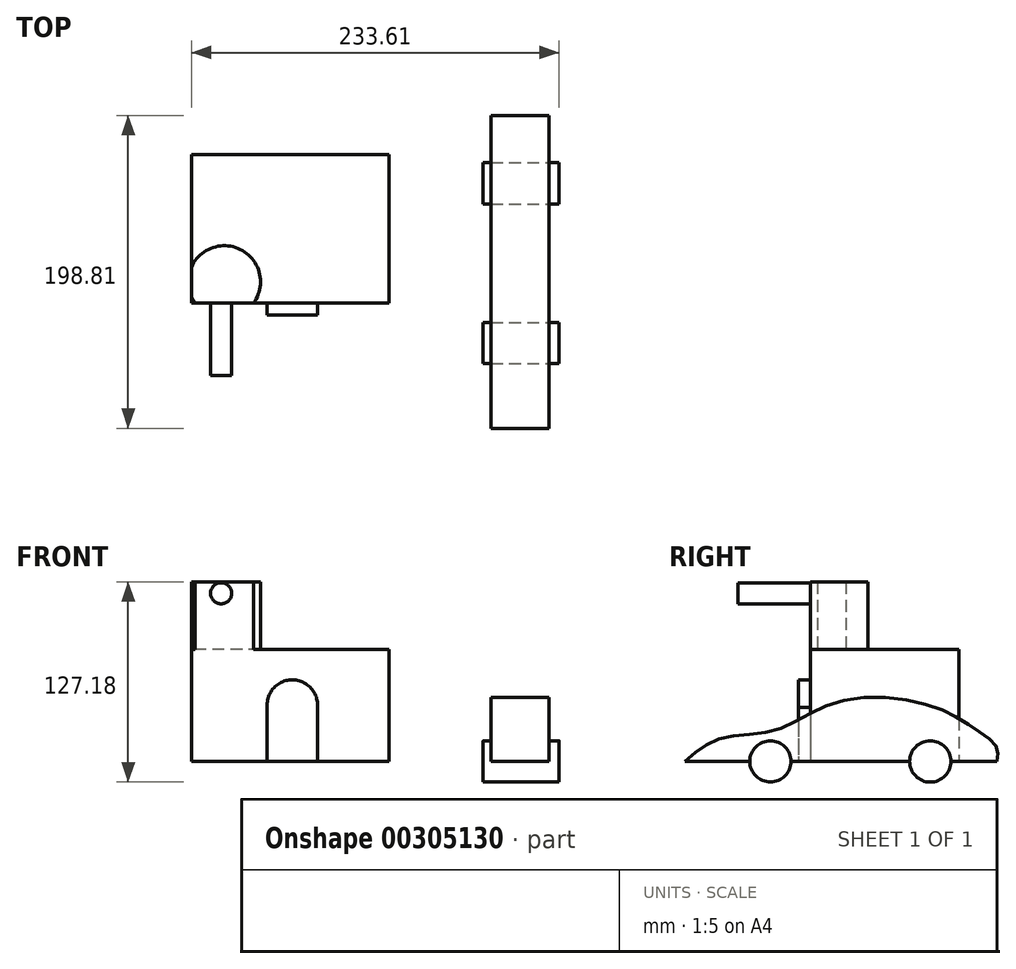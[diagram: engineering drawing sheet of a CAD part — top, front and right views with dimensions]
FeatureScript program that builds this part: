
annotation { "Feature Type Name" : "Feature", "Feature Type Description" : "" }
export const myFeature = defineFeature(function(context is Context, id is Id, definition is map)
    precondition{}
    {
        {
            var Q0;
            Q0=qCreatedBy(makeId("Top.planeOp"),FACE);
            var sketch = newSketch(context, id + "F0", { "sketchPlane" : qUnion([Q0])});
            skLineSegment(sketch, "E0.bottom", {"start": v(-64.2, 55.75) * mm, "end": v(61.5, 55.75) * mm});
            skLineSegment(sketch, "E0.top", {"start": v(-64.2, -38.63) * mm, "end": v(61.5, -38.63) * mm});
            skLineSegment(sketch, "E0.left", {"start": v(-64.2, 55.75) * mm, "end": v(-64.2, -38.63) * mm});
            skLineSegment(sketch, "E0.right", {"start": v(61.5, 55.75) * mm, "end": v(61.5, -38.63) * mm});
            skSolve(sketch);
        }
        {
            var Q0;
            Q0=makeQuery(id+"F0.imprint","IMPRINT",FACE,{"disambiguationData":[TD([[makeQuery(id+"F0.imprint","IMPRINT",EDGE,{"derivedFrom":sQuery(id+"F0.wireOp",EDGE,"E0.bottom")}),-1.0]])]});
            extrude(context, id + "F1", {"entities" : qUnion([Q0]), "depth" : 71.12 * mm});
        }
        {
            var Q0;
            Q0=makeQuery(id+"F1.opExtrude","SWEPT_FACE",FACE,{"disambiguationData":[OSD([sQuery(id+"F0.wireOp",EDGE,"E0.top")])]});
            var sketch = newSketch(context, id + "F2", { "sketchPlane" : qUnion([Q0])});
            skArc(sketch, "E1", {"start": v(15.92, 34.3) * mm, "mid": v(0.16, 51.86) * mm, "end": v(-15.95, 34.61) * mm});
            skLineSegment(sketch, "E2", {"start": v(-15.95, 37.12) * mm, "end": v(-15.95, 0) * mm});
            skLineSegment(sketch, "E3", {"start": v(15.92, 37.44) * mm, "end": v(15.92, 0) * mm});
            skLineSegment(sketch, "E4", {"start": v(-15.95, 0) * mm, "end": v(15.92, 0) * mm});
            skSolve(sketch);
        }
        {
            var Q0;
            Q0 = qSketchRegion(id + "F2", true);
            extrude(context, id + "F3", {"entities" : qUnion([Q0]), "operationType" : NewBodyOperationType.ADD, "depth" : 7.62 * mm});
        }
        {
            var Q0;
            Q0=makeQuery(id+"F1.opExtrude","CAP_FACE",FACE,{"disambiguationData":[OSD([sQuery(id+"F0.wireOp",EDGE,"E0.bottom"),sQuery(id+"F0.wireOp",EDGE,"E0.top"),sQuery(id+"F0.wireOp",EDGE,"E0.left"),sQuery(id+"F0.wireOp",EDGE,"E0.right")])],"isStart":false});
            var sketch = newSketch(context, id + "F4", { "sketchPlane" : qUnion([Q0])});
            skCircle(sketch, "E5", {"center": v(-43.2, -25.05) * mm, "radius": 22.93 * mm});
            skSolve(sketch);
        }
        {
            var Q0;
            {var subQ0=sQuery(id+"F4.wireOp",EDGE,"E5");var subQ1=makeQuery(id+"F1.opExtrude","CAP_EDGE",EDGE,{"disambiguationData":[OSD([sQuery(id+"F0.wireOp",EDGE,"E0.left")])],"isStart":false});var subQ2=makeQuery(id+"F4.imprint","INTERSECT",VERTEX,{"disambiguationData":[OD(0.0)],"derivedFrom":[subQ1,subQ0]});Q0=makeQuery(id+"F4.imprint","IMPRINT",FACE,{"disambiguationData":[TD([[makeQuery(id+"F4.imprint","IMPRINT",EDGE,{"disambiguationData":[TD([[subQ2,-1.0]])],"derivedFrom":subQ0}),1.0]])]});}
            extrude(context, id + "F5", {"entities" : qUnion([Q0]), "operationType" : NewBodyOperationType.ADD, "depth" : 42.93 * mm});
        }
        {
            var Q0;
            {var subQ0=sQuery(id+"F0.wireOp",EDGE,"E0.top");Q0=makeQuery(id+"F5.boolean.opBoolean","MERGE",FACE,{"derivedFrom":[makeQuery(id+"F1.opExtrude","SWEPT_FACE",FACE,{"disambiguationData":[OSD([subQ0])]}),makeQuery(id+"F5.opExtrude","SWEPT_FACE",FACE,{"disambiguationData":[OSD([subQ0])]})]});}
            var sketch = newSketch(context, id + "F6", { "sketchPlane" : qUnion([Q0])});
            skCircle(sketch, "E6", {"center": v(-45.26, 106.82) * mm, "radius": 6.7 * mm});
            skSolve(sketch);
        }
        {
            var Q0;
            Q0=makeQuery(id+"F6.imprint","IMPRINT",FACE,{"disambiguationData":[TD([[makeQuery(id+"F6.imprint","IMPRINT",EDGE,{"derivedFrom":sQuery(id+"F6.wireOp",EDGE,"E6")}),1.0]])]});
            extrude(context, id + "F7", {"entities" : qUnion([Q0]), "operationType" : NewBodyOperationType.ADD, "depth" : 45.97 * mm});
        }
        {
            var Q0;
            Q0=qCreatedBy(makeId("Right.planeOp"),FACE);
            cPlane(context, id + "F8", {"entities" : qUnion([Q0]), "cplaneType" : CPlaneType.OFFSET, "offset" : 126.24 * mm, "width" : 152.4 * mm, "height" : 152.4 * mm});
        }
        {
            var Q0;
            Q0=qCreatedBy(id+"F8.planeOp",FACE);
            var sketch = newSketch(context, id + "F9", { "sketchPlane" : qUnion([Q0])});
            skFitSpline(sketch, "E7", {"points": [v(-118.16, 0) * mm, v(-95.54, 14.65) * mm, v(-59.69, 20.2) * mm, v(-22.13, 37.7) * mm, v(37.2, 35.57) * mm, v(66.65, 20.2) * mm, v(79.89, 9.1) * mm, v(79.89, 0) * mm], "startDerivative": vector(149.82, 131.98) * mm, "endDerivative": vector(-25.14, -119.12) * mm});
            skFitSpline(sketch, "E8", {"points": [v(-118.16, 0) * mm, v(79.89, 0) * mm], "startDerivative": vector(198.05, 0) * mm, "endDerivative": vector(198.05, 0) * mm});
            skSolve(sketch);
        }
        {
            var Q0;
            Q0=makeQuery(id+"F9.imprint","IMPRINT",FACE,{"disambiguationData":[TD([[makeQuery(id+"F9.imprint","IMPRINT",EDGE,{"derivedFrom":sQuery(id+"F9.wireOp",EDGE,"E7")}),-1.0]])]});
            extrude(context, id + "F10", {"entities" : qUnion([Q0]), "depth" : 36.83 * mm});
        }
        {
            var Q0;
            Q0=makeQuery(id+"F10.opExtrude","CAP_FACE",FACE,{"disambiguationData":[OSD([sQuery(id+"F9.wireOp",EDGE,"E7"),sQuery(id+"F9.wireOp",EDGE,"E8")])],"isStart":false});
            var sketch = newSketch(context, id + "F11", { "sketchPlane" : qUnion([Q0])});
            skCircle(sketch, "E9", {"center": v(-64, 0) * mm, "radius": 13.1 * mm});
            skCircle(sketch, "E10", {"center": v(37.58, 0) * mm, "radius": 13.13 * mm});
            skSolve(sketch);
        }
        {
            var Q0;
            {var subQ0=sQuery(id+"F11.wireOp",EDGE,"E9");var subQ1=makeQuery(id+"F10.opExtrude","CAP_EDGE",EDGE,{"disambiguationData":[OSD([sQuery(id+"F9.wireOp",EDGE,"E8")])],"isStart":false});var subQ2=makeQuery(id+"F11.imprint","INTERSECT",VERTEX,{"disambiguationData":[OD(0.0)],"derivedFrom":[subQ1,subQ0]});Q0=makeQuery(id+"F11.imprint","IMPRINT",FACE,{"disambiguationData":[TD([[makeQuery(id+"F11.imprint","IMPRINT",EDGE,{"disambiguationData":[TD([[subQ2,-1.0]])],"derivedFrom":subQ0}),1.0]])]});}
            var Q1;
            {var subQ0=sQuery(id+"F11.wireOp",EDGE,"E9");var subQ1=makeQuery(id+"F10.opExtrude","CAP_EDGE",EDGE,{"disambiguationData":[OSD([sQuery(id+"F9.wireOp",EDGE,"E8")])],"isStart":false});var subQ2=makeQuery(id+"F11.imprint","INTERSECT",VERTEX,{"disambiguationData":[OD(0.0)],"derivedFrom":[subQ1,subQ0]});Q1=makeQuery(id+"F11.imprint","IMPRINT",FACE,{"disambiguationData":[TD([[makeQuery(id+"F11.imprint","IMPRINT",EDGE,{"disambiguationData":[TD([[subQ2,1.0]])],"derivedFrom":subQ0}),1.0]])]});}
            var Q2;
            {var subQ0=sQuery(id+"F11.wireOp",EDGE,"E10");var subQ1=makeQuery(id+"F10.opExtrude","CAP_EDGE",EDGE,{"disambiguationData":[OSD([sQuery(id+"F9.wireOp",EDGE,"E8")])],"isStart":false});var subQ2=makeQuery(id+"F11.imprint","INTERSECT",VERTEX,{"disambiguationData":[OD(0.0)],"derivedFrom":[subQ1,subQ0]});Q2=makeQuery(id+"F11.imprint","IMPRINT",FACE,{"disambiguationData":[TD([[makeQuery(id+"F11.imprint","IMPRINT",EDGE,{"disambiguationData":[TD([[subQ2,1.0]])],"derivedFrom":subQ0}),1.0]])]});}
            var Q3;
            {var subQ0=sQuery(id+"F11.wireOp",EDGE,"E10");var subQ1=makeQuery(id+"F10.opExtrude","CAP_EDGE",EDGE,{"disambiguationData":[OSD([sQuery(id+"F9.wireOp",EDGE,"E8")])],"isStart":false});var subQ2=makeQuery(id+"F11.imprint","INTERSECT",VERTEX,{"disambiguationData":[OD(0.0)],"derivedFrom":[subQ1,subQ0]});Q3=makeQuery(id+"F11.imprint","IMPRINT",FACE,{"disambiguationData":[TD([[makeQuery(id+"F11.imprint","IMPRINT",EDGE,{"disambiguationData":[TD([[subQ2,-1.0]])],"derivedFrom":subQ0}),1.0]])]});}
            extrude(context, id + "F12", {"entities" : qUnion([Q0, Q1, Q2, Q3]), "operationType" : NewBodyOperationType.ADD, "oppositeDirection" : true, "depth" : 41.9 * mm, "hasSecondDirection" : true, "secondDirectionOppositeDirection" : false, "secondDirectionDepth" : 6.35 * mm});
        }
    });
